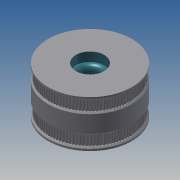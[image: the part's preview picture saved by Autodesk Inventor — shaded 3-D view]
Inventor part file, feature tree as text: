
AUTODESK INVENTOR PART (.ipt)
format: ipt  version: 2013 (Build 170138000, 138)  size: 817,152 bytes
history: native  units: mm
features: extrude x4, sketch x4, other x3, fillet x2
ambient origin geometry x8: Origin, YZ Plane, XZ Plane, XY Plane, X Axis, Y Axis, Z Axis, Center Point
bodies: Solid1 (feature_tree)
feature tree (13):
  other  "z idler pulley 2.iam"
  other  "100 pulley blank.ipt:1"
  other  "100 pulley blank.ipt:2"
  extrude  "Extrusion1"  Depth=10.0mm TaperAngle=0.0deg
  extrude  "Extrusion2"  Depth=10.0mm TaperAngle=0.0deg
  extrude  "Extrusion3"  Depth=7.0mm TaperAngle=0.0deg
  extrude  "Extrusion4"  Depth=7.0mm TaperAngle=0.0deg
  fillet  "Fillet1"  Radius=3.5mm
  fillet  "Fillet2"  Radius=3.5mm
  sketch  "Sketch1"  dims[d0=10.0mm d1=10.0mm d2=0.0mm]
  sketch  "Sketch2"  dims[d3=15.0mm d5=10.0mm d6=0.0mm]
  sketch  "Sketch3"  dims[d7=22.0mm d9=7.0mm d10=0.0mm]
  sketch  "Sketch4"  dims[d11=22.0mm d13=7.0mm d14=0.0mm d15=3.5mm d16=3.5mm]
